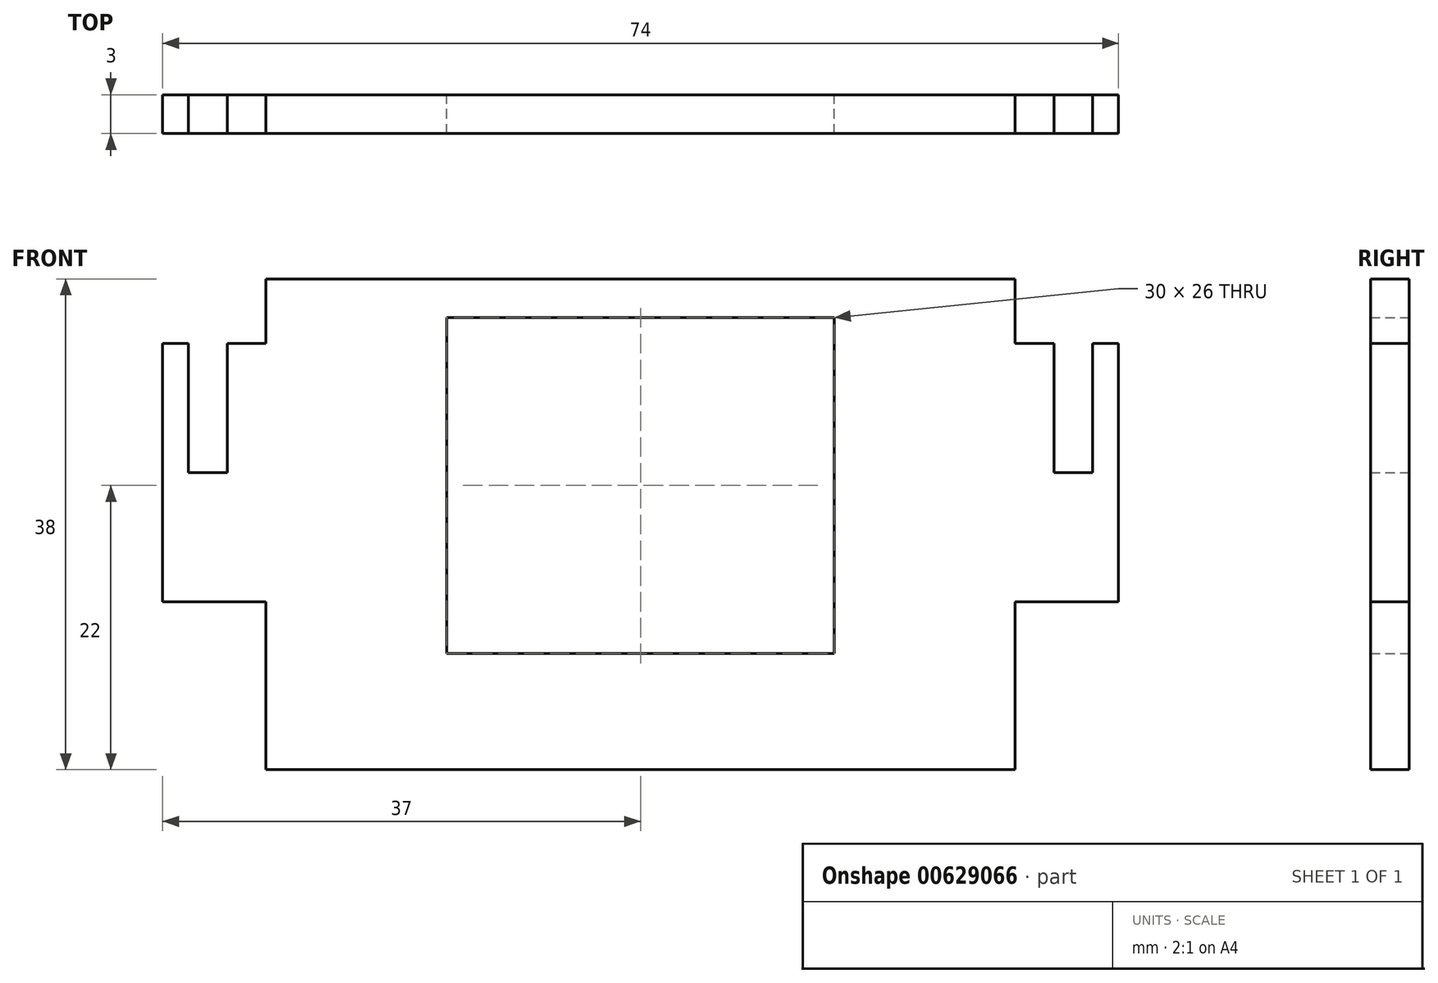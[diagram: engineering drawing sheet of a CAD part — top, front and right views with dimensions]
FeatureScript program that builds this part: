
annotation { "Feature Type Name" : "Feature", "Feature Type Description" : "" }
export const myFeature = defineFeature(function(context is Context, id is Id, definition is map)
    precondition{}
    {
        {
            var Q0;
            Q0=qCreatedBy(makeId("Front.planeOp"),FACE);
            var sketch = newSketch(context, id + "F0", { "sketchPlane" : qUnion([Q0])});
            skLineSegment(sketch, "E0", {"start": v(0, 72.53) * mm, "end": v(0, -57.7) * mm, "construction": true});
            skLineSegment(sketch, "E1", {"start": v(-78.53, 0) * mm, "end": v(80.65, 0) * mm, "construction": true});
            skLineSegment(sketch, "E2.bottom", {"start": v(-29, 28) * mm, "end": v(29, 28) * mm});
            skLineSegment(sketch, "E2.top", {"start": v(-29, -10) * mm, "end": v(29, -10) * mm});
            skLineSegment(sketch, "E2.left", {"start": v(-29, 28) * mm, "end": v(-29, 23) * mm});
            skLineSegment(sketch, "E2.right", {"start": v(29, 28) * mm, "end": v(29, 23) * mm});
            skLineSegment(sketch, "E3.bottom", {"start": v(-15, 25) * mm, "end": v(15, 25) * mm});
            skLineSegment(sketch, "E3.top", {"start": v(-15, -1) * mm, "end": v(15, -1) * mm});
            skLineSegment(sketch, "E3.left", {"start": v(-15, 25) * mm, "end": v(-15, -1) * mm});
            skLineSegment(sketch, "E3.right", {"start": v(15, 25) * mm, "end": v(15, -1) * mm});
            skLineSegment(sketch, "E4.top", {"start": v(-29, 3) * mm, "end": v(-37, 3) * mm});
            skLineSegment(sketch, "E4.right", {"start": v(-37, 23) * mm, "end": v(-37, 3) * mm});
            skLineSegment(sketch, "E5.trimOffspring", {"start": v(-29, 3) * mm, "end": v(-29, -10) * mm});
            skLineSegment(sketch, "E6.trimOffspring", {"start": v(-35, 23) * mm, "end": v(-37, 23) * mm});
            skLineSegment(sketch, "E7", {"start": v(-35, 23) * mm, "end": v(-35, 13) * mm});
            skLineSegment(sketch, "E8", {"start": v(-35, 13) * mm, "end": v(-32, 13) * mm});
            skLineSegment(sketch, "E9", {"start": v(-32, 13) * mm, "end": v(-32, 23) * mm});
            skLineSegment(sketch, "E10", {"start": v(-32, 23) * mm, "end": v(-29, 23) * mm});
            skLineSegment(sketch, "E11.MirrorCS", {"start": v(32, 13) * mm, "end": v(32, 23) * mm});
            skLineSegment(sketch, "E12.MirrorCS", {"start": v(35, 13) * mm, "end": v(32, 13) * mm});
            skLineSegment(sketch, "E13.MirrorCS", {"start": v(35, 23) * mm, "end": v(35, 13) * mm});
            skLineSegment(sketch, "E14.MirrorCS", {"start": v(35, 23) * mm, "end": v(37, 23) * mm});
            skLineSegment(sketch, "E15.MirrorCS", {"start": v(32, 23) * mm, "end": v(29, 23) * mm});
            skLineSegment(sketch, "E16.MirrorCS", {"start": v(37, 23) * mm, "end": v(37, 3) * mm});
            skLineSegment(sketch, "E17.MirrorCS", {"start": v(29, 3) * mm, "end": v(37, 3) * mm});
            skLineSegment(sketch, "E18.trimOffspring", {"start": v(29, 3) * mm, "end": v(29, -10) * mm});
            skSolve(sketch);
        }
        {
            var Q0;
            Q0=qSketchRegion(id+"F0",true);
            extrude(context, id + "F1", {"entities" : qUnion([Q0]), "endBound" : BoundingType.SYMMETRIC, "depth" : 3 * mm, "offsetDistance" : 25 * mm});
        }
    });
